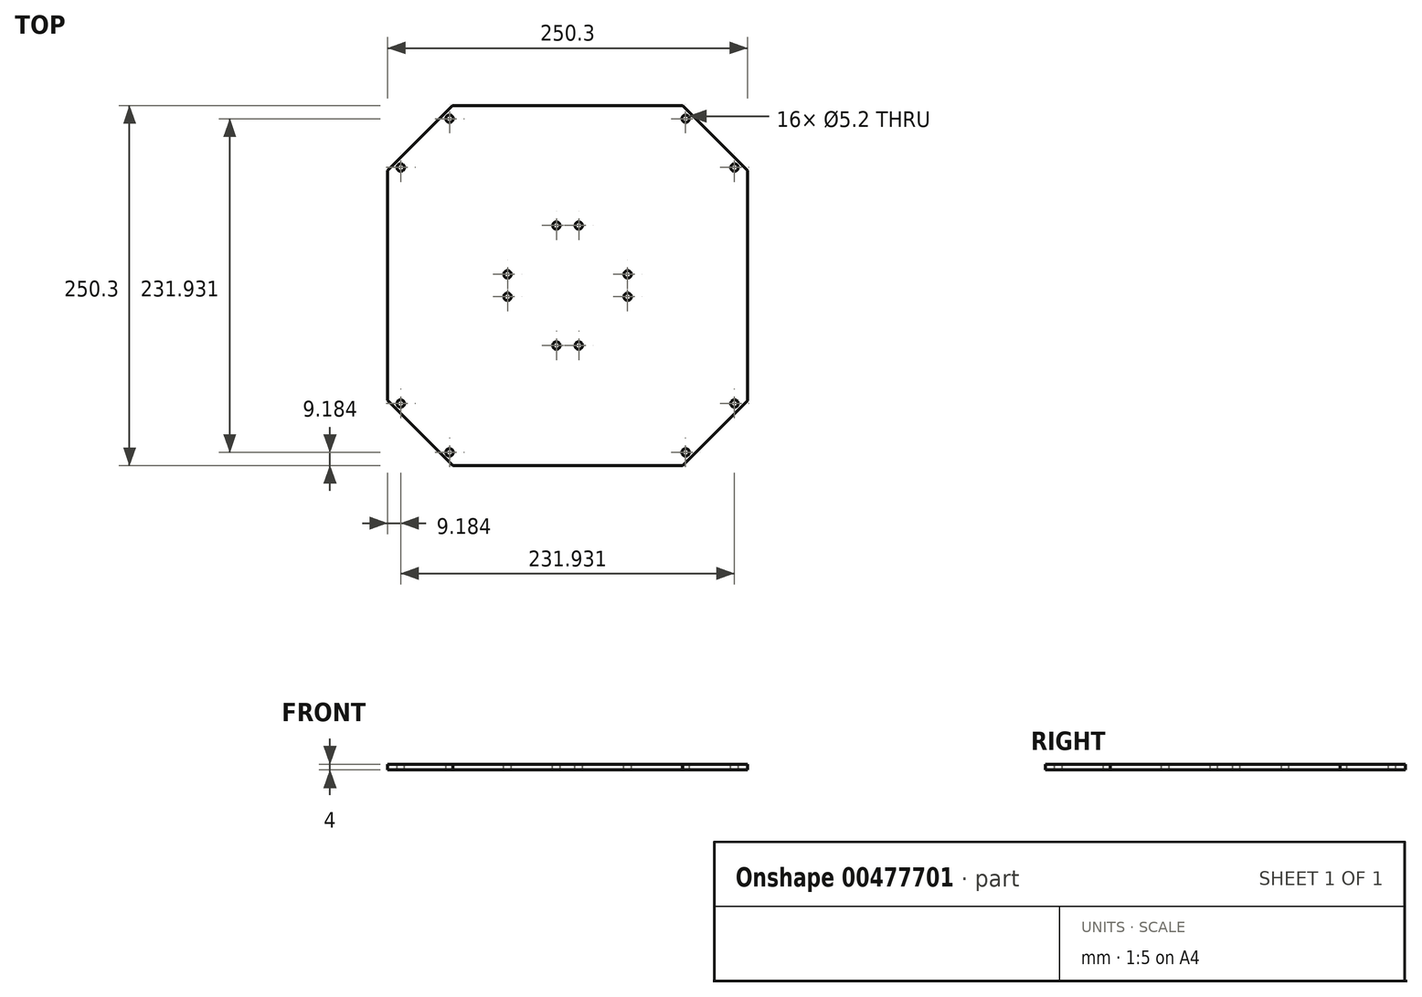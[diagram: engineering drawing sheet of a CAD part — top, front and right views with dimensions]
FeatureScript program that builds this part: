
annotation { "Feature Type Name" : "Feature", "Feature Type Description" : "" }
export const myFeature = defineFeature(function(context is Context, id is Id, definition is map)
    precondition{}
    {
        {
            var Q0;
            Q0=qCreatedBy(makeId("Top.planeOp"),FACE);
            var sketch = newSketch(context, id + "F0", { "sketchPlane" : qUnion([Q0])});
            skLineSegment(sketch, "E0", {"start": v(-102.53, 102.53) * mm, "end": v(102.53, -102.53) * mm, "construction": true});
            skLineSegment(sketch, "E1", {"start": v(-100.97, -100.97) * mm, "end": v(102.5, 102.5) * mm, "construction": true});
            skLineSegment(sketch, "E2", {"start": v(0, 0) * mm, "end": v(0, 125.15) * mm, "construction": true});
            skLineSegment(sketch, "E3", {"start": v(102.5, 102.5) * mm, "end": v(79.85, 125.15) * mm});
            skLineSegment(sketch, "E4", {"start": v(79.85, 125.15) * mm, "end": v(-79.91, 125.15) * mm});
            skLineSegment(sketch, "E5", {"start": v(-79.91, 125.15) * mm, "end": v(-102.53, 102.53) * mm});
            skLineSegment(sketch, "E6.MirrorCS", {"start": v(102.5, 102.5) * mm, "end": v(125.15, 79.85) * mm});
            skLineSegment(sketch, "E7.MirrorCS", {"start": v(125.15, 79.85) * mm, "end": v(125.15, -79.91) * mm});
            skLineSegment(sketch, "E8.MirrorCS", {"start": v(125.15, -79.91) * mm, "end": v(102.53, -102.53) * mm});
            skLineSegment(sketch, "E9.MirrorCS", {"start": v(-125.15, 79.91) * mm, "end": v(-102.53, 102.53) * mm});
            skLineSegment(sketch, "E10.MirrorCS", {"start": v(-125.15, -79.85) * mm, "end": v(-125.15, 79.91) * mm});
            skLineSegment(sketch, "E11.MirrorCS", {"start": v(-102.5, -102.5) * mm, "end": v(-125.15, -79.85) * mm});
            skLineSegment(sketch, "E12.MirrorCS", {"start": v(-102.5, -102.5) * mm, "end": v(-79.85, -125.15) * mm});
            skLineSegment(sketch, "E13.MirrorCS", {"start": v(-79.85, -125.15) * mm, "end": v(79.91, -125.15) * mm});
            skLineSegment(sketch, "E14.MirrorCS", {"start": v(79.91, -125.15) * mm, "end": v(102.53, -102.53) * mm});
            skSolve(sketch);
        }
        {
            var Q0;
            Q0=makeQuery(id+"F0.imprint","IMPRINT",FACE,{"disambiguationData":[TD([[makeQuery(id+"F0.imprint","IMPRINT",EDGE,{"derivedFrom":sQuery(id+"F0.wireOp",EDGE,"wkNUffIB-qnCA-ifZx-wQDp-ZMm1OhZD6AcE")}),-1.0]])]});
            var Q1;
            Q1=makeQuery(id+"F0.imprint","IMPRINT",FACE,{"disambiguationData":[TD([[makeQuery(id+"F0.imprint","IMPRINT",EDGE,{"derivedFrom":sQuery(id+"F0.wireOp",EDGE,"E3")}),1.0]])]});
            extrude(context, id + "F1", {"entities" : qUnion([Q0, Q1]), "depth" : 4 * mm});
        }
        {
            var Q0;
            Q0=makeQuery(id+"F1.opExtrude","CAP_FACE",FACE,{"disambiguationData":[OSD([sQuery(id+"F0.wireOp",EDGE,"E3"),sQuery(id+"F0.wireOp",EDGE,"E4"),sQuery(id+"F0.wireOp",EDGE,"E5"),sQuery(id+"F0.wireOp",EDGE,"E6.MirrorCS"),sQuery(id+"F0.wireOp",EDGE,"E7.MirrorCS"),sQuery(id+"F0.wireOp",EDGE,"E8.MirrorCS"),sQuery(id+"F0.wireOp",EDGE,"E9.MirrorCS"),sQuery(id+"F0.wireOp",EDGE,"E10.MirrorCS"),sQuery(id+"F0.wireOp",EDGE,"E11.MirrorCS"),sQuery(id+"F0.wireOp",EDGE,"E12.MirrorCS"),sQuery(id+"F0.wireOp",EDGE,"E13.MirrorCS"),sQuery(id+"F0.wireOp",EDGE,"E14.MirrorCS")])],"isStart":false});
            var sketch = newSketch(context, id + "F2", { "sketchPlane" : qUnion([Q0])});
            skLineSegment(sketch, "E15", {"start": v(0, 0) * mm, "end": v(0, 125.15) * mm, "construction": true});
            skLineSegment(sketch, "E16", {"start": v(0, 0) * mm, "end": v(-125.15, 0) * mm, "construction": true});
            skLineSegment(sketch, "E17", {"start": v(0, 0) * mm, "end": v(-102.53, 102.53) * mm, "construction": true});
            skCircle(sketch, "E18", {"center": v(-7.78, 41.72) * mm, "radius": 2.6 * mm});
            skLineSegment(sketch, "E19", {"start": v(0, 0) * mm, "end": v(-102.5, -102.5) * mm, "construction": true});
            skLineSegment(sketch, "E20.MirrorCS", {"start": v(0, 0) * mm, "end": v(102.53, -102.53) * mm, "construction": true});
            skCircle(sketch, "E21.MirrorC", {"center": v(-41.72, 7.78) * mm, "radius": 2.6 * mm});
            skCircle(sketch, "E22.MirrorC", {"center": v(7.78, -41.72) * mm, "radius": 2.6 * mm});
            skCircle(sketch, "E23.MirrorC", {"center": v(41.72, -7.78) * mm, "radius": 2.6 * mm});
            skCircle(sketch, "E24.1.0", {"center": v(41.72, 7.78) * mm, "radius": 2.6 * mm});
            skCircle(sketch, "E24.1.1", {"center": v(7.78, 41.72) * mm, "radius": 2.6 * mm});
            skCircle(sketch, "E24.1.2", {"center": v(-41.72, -7.78) * mm, "radius": 2.6 * mm});
            skCircle(sketch, "E24.1.3", {"center": v(-7.78, -41.72) * mm, "radius": 2.6 * mm});
            skPoint(sketch, "E24.center", {"position": v(0, 0) * mm});
            skLineSegment(sketch, "E24.anchor1", {"start": v(0, 0) * mm, "end": v(-7.78, 41.72) * mm, "construction": true});
            skLineSegment(sketch, "E24.anchor2", {"start": v(0, 0) * mm, "end": v(41.72, 7.78) * mm, "construction": true});
            skSolve(sketch);
        }
        {
            var Q0;
            Q0=qSketchRegion(id+"F2",true);
            extrude(context, id + "F3", {"entities" : qUnion([Q0]), "operationType" : NewBodyOperationType.REMOVE, "oppositeDirection" : true, "depth" : 20 * mm});
        }
        {
            var Q0;
            Q0=makeQuery(id+"F2.imprint","IMPRINT",FACE,{"disambiguationData":[TD([[makeQuery(id+"F2.imprint","IMPRINT",EDGE,{"derivedFrom":sQuery(id+"F2.wireOp",EDGE,"E18")}),-1.0]])]});
            var sketch = newSketch(context, id + "F4", { "sketchPlane" : qUnion([Q0])});
            skLineSegment(sketch, "E25.0", {"start": v(0, 0) * mm, "end": v(0, 125.15) * mm, "construction": true});
            skLineSegment(sketch, "E25.1", {"start": v(0, 0) * mm, "end": v(-102.53, 102.53) * mm, "construction": true});
            skLineSegment(sketch, "E25.2", {"start": v(0, 0) * mm, "end": v(-125.15, 0) * mm, "construction": true});
            skLineSegment(sketch, "E25.3", {"start": v(0, 0) * mm, "end": v(-102.5, -102.5) * mm, "construction": true});
            skLineSegment(sketch, "E25.4", {"start": v(0, 0) * mm, "end": v(102.53, -102.53) * mm, "construction": true});
            skCircle(sketch, "E26", {"center": v(-82.02, 115.97) * mm, "radius": 2.6 * mm});
            skCircle(sketch, "E27.MirrorC", {"center": v(-115.97, 82.02) * mm, "radius": 2.6 * mm});
            skCircle(sketch, "E28.MirrorC", {"center": v(82.02, -115.97) * mm, "radius": 2.6 * mm});
            skCircle(sketch, "E29.MirrorC", {"center": v(115.97, -82.02) * mm, "radius": 2.6 * mm});
            skCircle(sketch, "E30.1.0", {"center": v(82.02, 115.97) * mm, "radius": 2.6 * mm});
            skCircle(sketch, "E30.1.1", {"center": v(115.97, 82.02) * mm, "radius": 2.6 * mm});
            skCircle(sketch, "E30.1.2", {"center": v(-115.97, -82.02) * mm, "radius": 2.6 * mm});
            skCircle(sketch, "E30.1.3", {"center": v(-82.02, -115.97) * mm, "radius": 2.6 * mm});
            skPoint(sketch, "E30.center", {"position": v(0, 0) * mm});
            skLineSegment(sketch, "E30.anchor1", {"start": v(0, 0) * mm, "end": v(-115.97, 82.02) * mm, "construction": true});
            skLineSegment(sketch, "E30.anchor2", {"start": v(0, 0) * mm, "end": v(82.02, 115.97) * mm, "construction": true});
            skSolve(sketch);
        }
        {
            var Q0;
            Q0=qSketchRegion(id+"F4",true);
            extrude(context, id + "F5", {"entities" : qUnion([Q0]), "operationType" : NewBodyOperationType.REMOVE, "endBound" : BoundingType.THROUGH_ALL, "oppositeDirection" : true, "depth" : 25 * mm});
        }
    });
